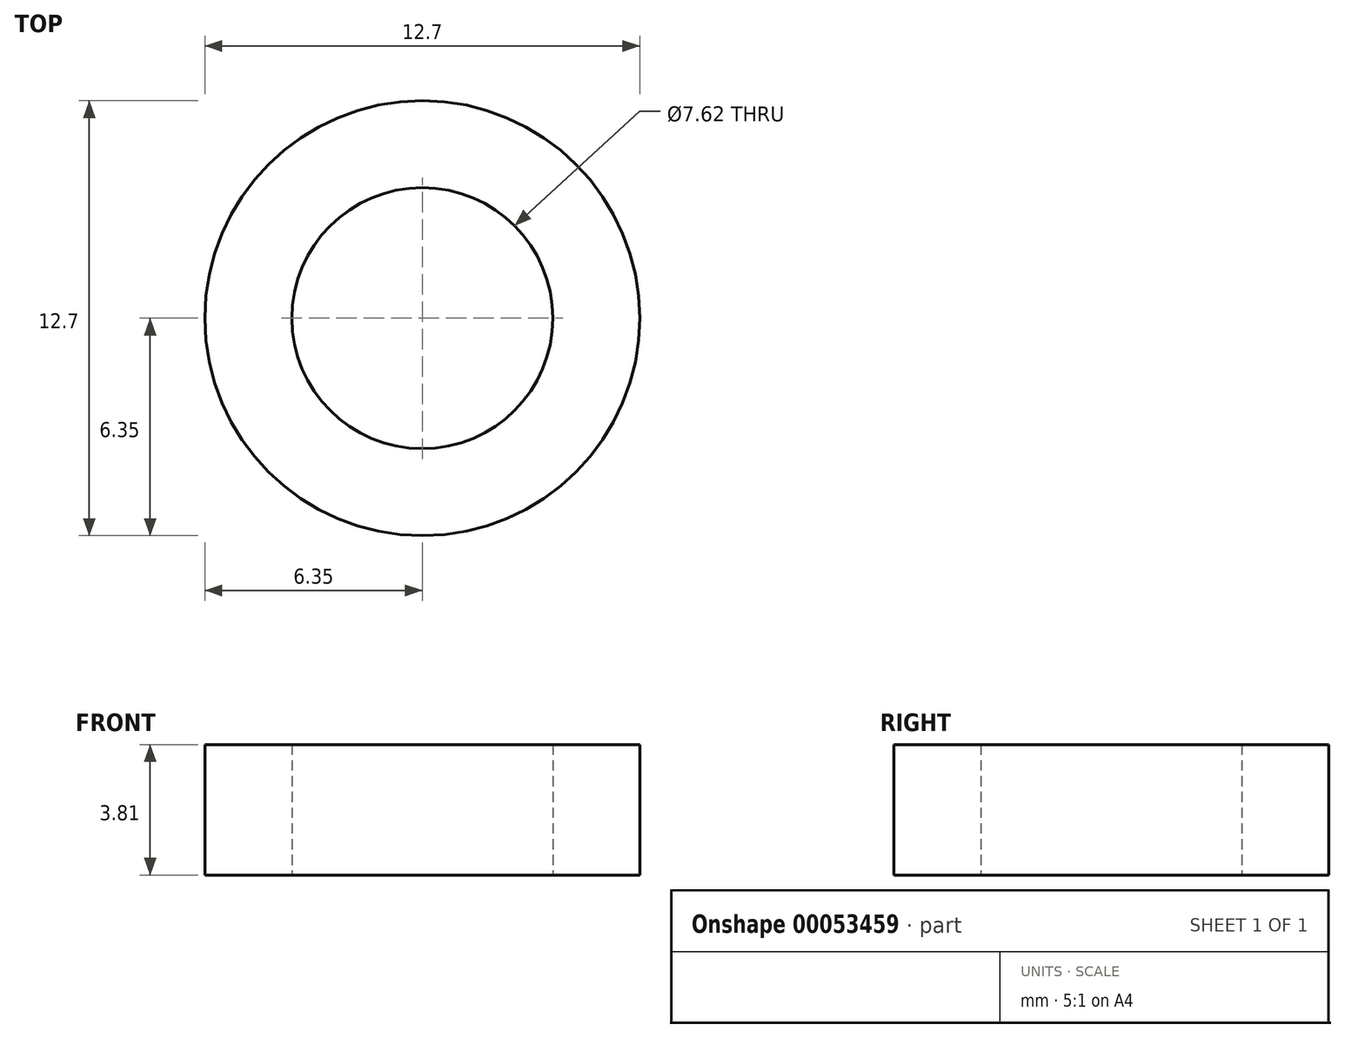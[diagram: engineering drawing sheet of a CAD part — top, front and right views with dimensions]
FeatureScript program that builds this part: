
annotation { "Feature Type Name" : "Feature", "Feature Type Description" : "" }
export const myFeature = defineFeature(function(context is Context, id is Id, definition is map)
    precondition{}
    {
        {
            var Q0;
            Q0=qCreatedBy(makeId("Top.planeOp"),FACE);
            var sketch = newSketch(context, id + "F0", { "sketchPlane" : qUnion([Q0])});
            skCircle(sketch, "E0", {"center": v(0, 0) * mm, "radius": 6.35 * mm});
            skCircle(sketch, "E1", {"center": v(0, 0) * mm, "radius": 3.81 * mm});
            skSolve(sketch);
        }
        {
            var Q0;
            Q0 = qSketchRegion(id + "F0", true);
            extrude(context, id + "F1", {"entities" : qUnion([Q0]), "depth" : 3.8 * mm});
        }
    });
